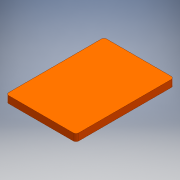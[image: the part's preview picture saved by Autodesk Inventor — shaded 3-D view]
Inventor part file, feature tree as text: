
AUTODESK INVENTOR PART (.ipt)
format: ipt  version: 2016 (Build 200138000, 138)  size: 123,904 bytes
history: native  units: mm
features: extrude x2, sketch x2
ambient origin geometry x8: Origin, YZ Plane, XZ Plane, XY Plane, X Axis, Y Axis, Z Axis, Center Point
bodies: Solid1 (feature_tree)
feature tree (4):
  extrude  "base"  Depth=50.0mm
  extrude  "Extrusion2"  Depth=2.0mm
  sketch  "Sketch1"  dims[d0=70.0mm d1=50.0mm]
  sketch  "Sketch3"  dims[d2=35.0mm d3=25.0mm d4=2.0mm d5=5.0mm d6=0.0mm d7=2.65mm d8=2.65mm d9=2.65mm d10=2.65mm d11=2.65mm d12=15.0mm d13=15.0mm d14=15.0mm d15=15.0mm d16=2.0mm d17=0.0mm]
